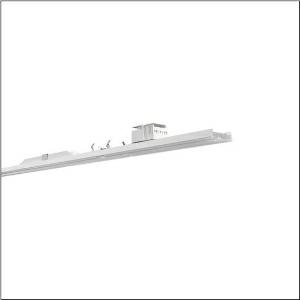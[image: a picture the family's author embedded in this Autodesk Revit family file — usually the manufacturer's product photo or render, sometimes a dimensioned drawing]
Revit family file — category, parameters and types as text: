
# Revit family: licross_r__11_recessed_ho_51tl18cn4cxld_d583
name_source: partatom
category: Lighting Fixtures
units: mm (PartAtom-declared; Revit-internal decimal feet)

## family parameters
Cut with Voids When Loaded = No
Host = Face
Light Source = No
Part Type = Normal
Room Calculation Point = No
Round Connector Dimension = Use Diameter
Shared = No

## types (1)
- --- (1 x LED, 3370 lm, 21.5 W, 4000K)
    Apparent Load = 22 VA
    CIE Flux Codes = 78 94 99 100 100
    Color Rendering = 80
    Color Temperature = 4000K
    Default Elevation = 1800 mm
    Description = Licross® 11 Recessed HOluminaire insert, length: 1.500mm, width: 66mm, height: 67mm, LED rated luminous flux: 12.000lm, light colour: 840, control gear: ON/OFF Multilumen, CLOi, control gear: ECG Multilumen, with plug, 6-pole, with phase selection, mains connection: 220..240V, AC/DC, 0/50..60Hz, without changeover relay, for emergency light function, for central battery installations according to DIN EN 60598-2-22, halogen-free wiring, primary optical cover: cover, of PMMA, light emission: direct distribution, protection rating (complete): IP40, insulation class (complete): insulation class I (protective earthing), certification: CE, ENEC, VDE, protection symbol: D if used in an environment without relevant dust loads with corresponding accessories, permissible ambient temperature for indoor applications: -35..+35°C, standard: EN 60598-2-22, reducing of maximum allowable ambient temperature of 5°C with ceiling mounting, corresponds to IFS (International Featured Standards) requirements for safety and quality in the food industry, packaging unit: 1 piece
    Height = 58 mm
    Lamp = 1 x LED
    Lamp Light Flux = 3370 lm
    Lamp Power = 21.5 W
    Lamp count = 1
    Length = 1500 mm
    Luminous efficacy = 157 lm/W
    Manufacturer = Siteco
    ModVariant = No
    Model = 51TL18CN4CXLD
    Mounting Place = Ceiling
    Mounting Type = Pendant
    Number of Poles = 1
    OnlyDefault = Yes
    Power Factor = 1
    Product Name = Licross® 11 Recessed HO
    Product group = luminaire insert
    ProductGroupID = 902
    Protection Class = Protection class I
    Protection Degree = IP 40
    RLX_Detail_Level = 1
    RlxData = <blob elided: 20537 chars, md5=9c850238>
    Socket = socket
    Standby Power = 0 W
    System Light Flux = 3370 lm
    System Power = 22 W
    Type Comments = : DC mode (central or group accumulator) initial emergency light level
    Type Image = l_1266722.jpg
    URL = http://relux.com
    VarID = @adj_134227
    Voltage = 0 V
    Weight = 0.00 kg
    Width = 66 mm

## geometry (parser evidence)
native form markers: Blend x4, Sweep x11
no freeform markers — native parametric forms only
